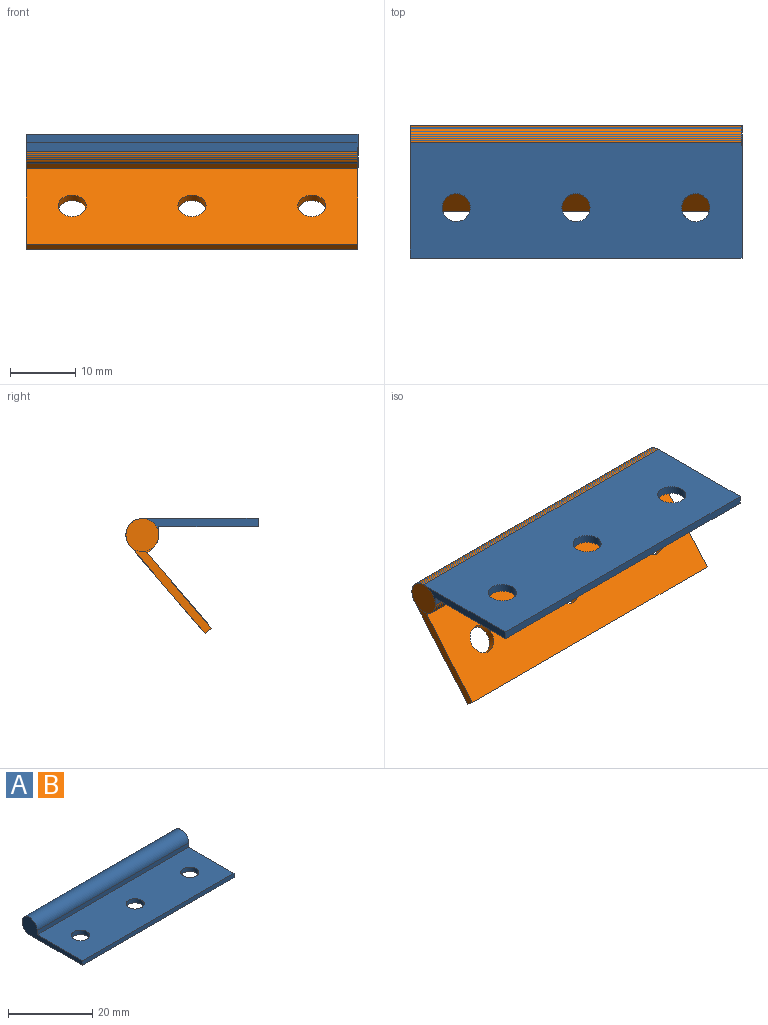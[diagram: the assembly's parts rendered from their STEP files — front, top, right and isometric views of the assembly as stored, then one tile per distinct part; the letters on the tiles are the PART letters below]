
ASSEMBLY  parts=2 mates=1
PART A: 10 faces, bbox 51.1x20.3x5.1 mm
  f0: plane 51.05x1.27mm, normal (0,-1,0), area 64.8mm2, adj f1,f4,f5,f6
  f1: plane 51.05x15.24mm, normal (0,0,1), area 734.1mm2, adj f0,f2,f5,f6,f7,f8,f9
  f2: plane 51.05x1.27mm, normal (0,-1,0), area 64.8mm2, adj f1,f3,f5,f6
  f3: plane 51.05x17.78mm, normal (0,0,-1), area 863.8mm2, adj f2,f4,f5,f6,f7,f8,f9
  f4: cylinder r=2.54mm len=51.05mm, axis (-1,0,0), area 611.1mm2, adj f0,f3,f5,f6
  f5: plane 20.32x5.08mm, normal (1,0,0), area 41mm2, adj f0,f1,f2,f3,f4
  f6: plane 20.32x5.08mm, normal (-1,0,0), area 41mm2, adj f0,f1,f2,f3,f4
  f7: cylinder r=2.16mm len=4.32mm, axis (0,0,1), area 17.2mm2, adj f1,f3
  f8: cylinder r=2.16mm len=4.32mm, axis (0,0,1), area 17.2mm2, adj f1,f3
  f9: cylinder r=2.16mm len=4.32mm, axis (0,0,1), area 17.2mm2, adj f1,f3
PART B: same geometry as A
PLACE A rot(axis=(0,1,0),180deg) t=(29.72,9.93,-2.29)mm fixed
PLACE B rot(axis=(1,0,0),49.4deg) t=(-21.34,10.09,-2.65)mm
MATE revolute A.f4 <-> B.f4  axis (1,0,0) through (4.19,7.64,-3.56)mm
